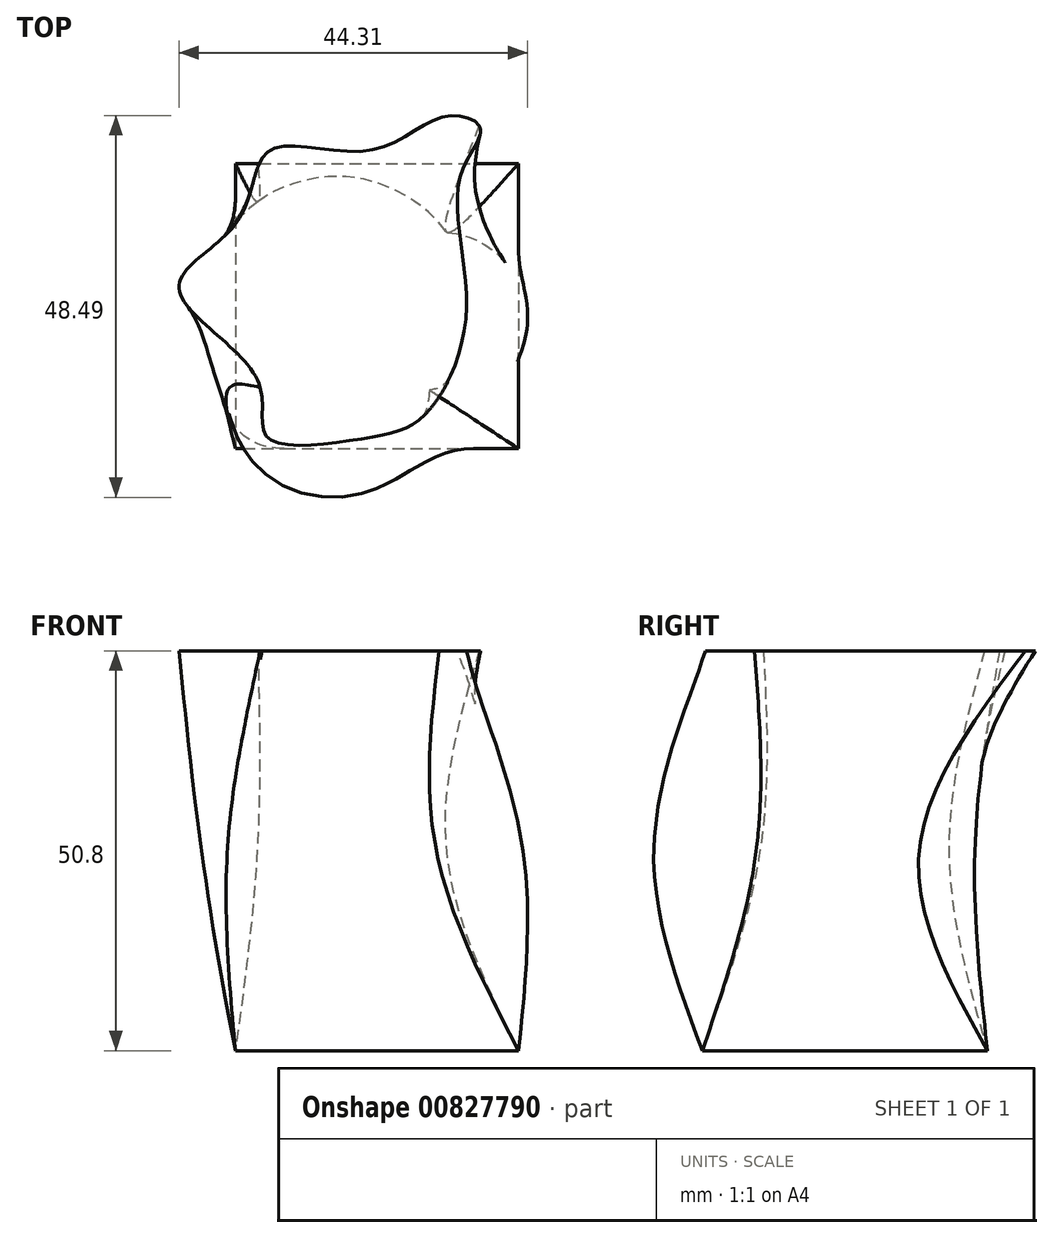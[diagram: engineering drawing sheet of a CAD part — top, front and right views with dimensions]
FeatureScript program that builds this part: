
annotation { "Feature Type Name" : "Feature", "Feature Type Description" : "" }
export const myFeature = defineFeature(function(context is Context, id is Id, definition is map)
    precondition{}
    {
        {
            var Q0;
            Q0=qCreatedBy(makeId("Top.planeOp"),FACE);
            cPlane(context, id + "F0", {"entities" : qUnion([Q0]), "cplaneType" : CPlaneType.OFFSET, "offset" : 25.4 * mm, "width" : 152.4 * mm, "height" : 152.4 * mm});
        }
        {
            var Q0;
            Q0=qCreatedBy(id+"F0.planeOp",FACE);
            cPlane(context, id + "F1", {"entities" : qUnion([Q0]), "cplaneType" : CPlaneType.OFFSET, "offset" : 25.4 * mm, "width" : 152.4 * mm, "height" : 152.4 * mm});
        }
        {
            var Q0;
            Q0=qCreatedBy(makeId("Top.planeOp"),FACE);
            var sketch = newSketch(context, id + "F2", { "sketchPlane" : qUnion([Q0])});
            skLineSegment(sketch, "E0.bottom", {"start": v(-17.02, 15.87) * mm, "end": v(18.94, 15.87) * mm});
            skLineSegment(sketch, "E0.top", {"start": v(-17.02, -20.34) * mm, "end": v(18.94, -20.34) * mm});
            skLineSegment(sketch, "E0.left", {"start": v(-17.02, 15.87) * mm, "end": v(-17.02, -20.34) * mm});
            skLineSegment(sketch, "E0.right", {"start": v(18.94, 15.87) * mm, "end": v(18.94, -20.34) * mm});
            skSolve(sketch);
        }
        {
            var Q0;
            Q0=qCreatedBy(id+"F0.planeOp",FACE);
            var sketch = newSketch(context, id + "F3", { "sketchPlane" : qUnion([Q0])});
            skArc(sketch, "E1", {"start": v(8.51, -13.5) * mm, "mid": v(19.48, -3.77) * mm, "end": v(9.75, 7.2) * mm});
            skArc(sketch, "E2", {"start": v(-18.03, -13) * mm, "mid": v(-5, -26.52) * mm, "end": v(8.51, -13.5) * mm});
            skArc(sketch, "E3", {"start": v(9.75, 7.2) * mm, "mid": v(-14.24, 10.99) * mm, "end": v(-18.03, -13) * mm});
            skSolve(sketch);
        }
        {
            var Q0;
            Q0=qCreatedBy(id+"F1.planeOp",FACE);
            var sketch = newSketch(context, id + "F4", { "sketchPlane" : qUnion([Q0])});
            skFitSpline(sketch, "E4", {"points": [v(11.54, 14.22) * mm, v(12.3, -3.12) * mm, v(6.95, -16.13) * mm, v(0, -18.92) * mm, v(-12.94, -18.94) * mm, v(-14.23, -11.6) * mm, v(-24.2, 0) * mm, v(-16.68, 8.64) * mm, v(-12.69, 17.53) * mm, v(0, 17.53) * mm, v(9.75, 21.87) * mm, v(14.09, 20.34) * mm, v(11.54, 14.22) * mm]});
            skSolve(sketch);
        }
        {
            var Q0;
            Q0=makeQuery(id+"F4.imprint","IMPRINT",FACE,{"disambiguationData":[TD([[makeQuery(id+"F4.imprint","IMPRINT",EDGE,{"derivedFrom":sQuery(id+"F4.wireOp",EDGE,"E4")}),-1.0]])]});
            var Q1;
            Q1=makeQuery(id+"F3.imprint","IMPRINT",FACE,{"disambiguationData":[TD([[makeQuery(id+"F3.imprint","IMPRINT",EDGE,{"derivedFrom":sQuery(id+"F3.wireOp",EDGE,"E1")}),1.0]])]});
            var Q2;
            Q2=makeQuery(id+"F2.imprint","IMPRINT",FACE,{"disambiguationData":[TD([[makeQuery(id+"F2.imprint","IMPRINT",EDGE,{"derivedFrom":sQuery(id+"F2.wireOp",EDGE,"E0.bottom")}),-1.0]])]});
            loft(context, id + "F5", {"sheetProfilesArray" : [{ "sheetProfileEntities" : qUnion([Q0]) }, { "sheetProfileEntities" : qUnion([Q1]) }, { "sheetProfileEntities" : qUnion([Q2]) }]});
        }
    });
